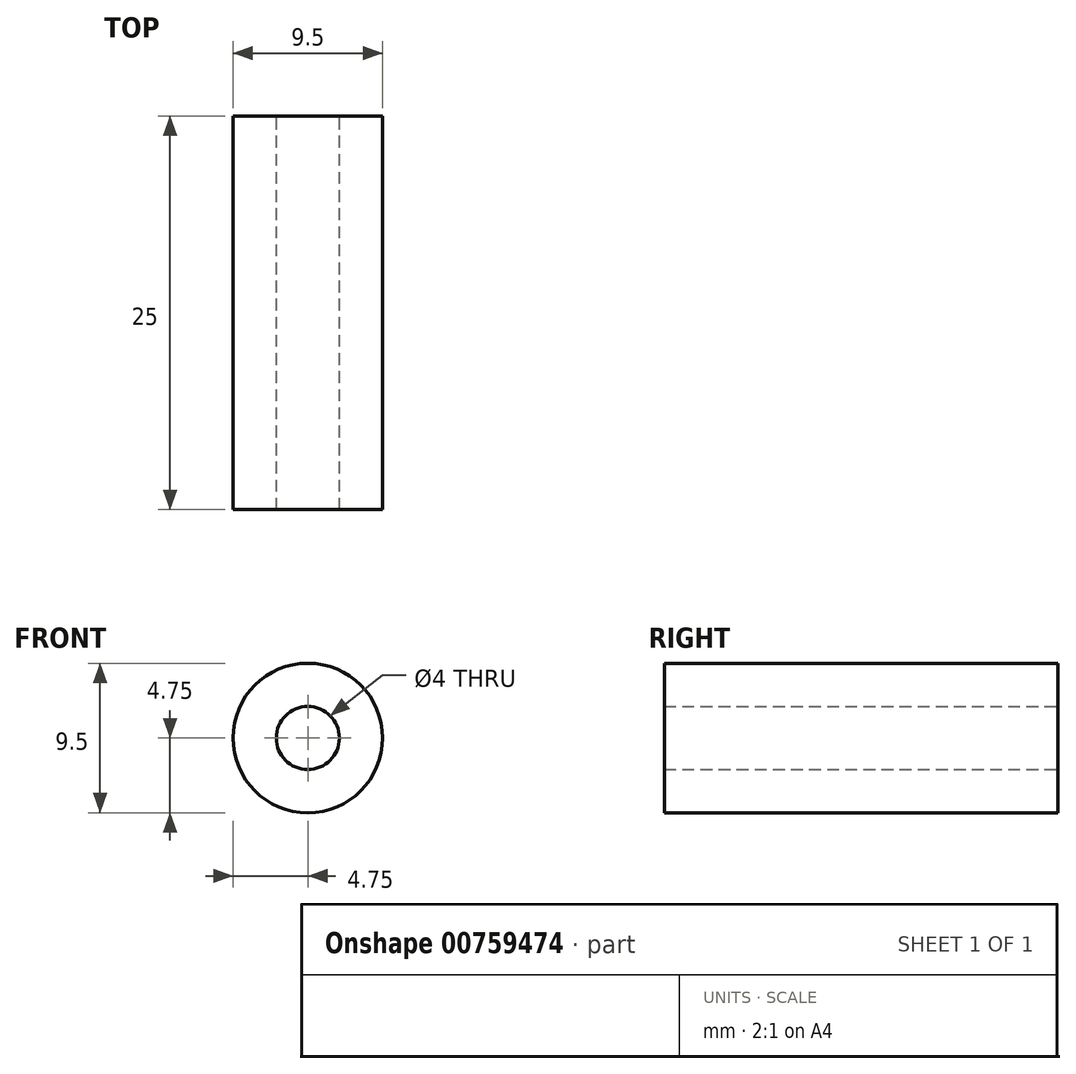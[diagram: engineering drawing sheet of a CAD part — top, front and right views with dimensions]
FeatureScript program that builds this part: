
annotation { "Feature Type Name" : "Feature", "Feature Type Description" : "" }
export const myFeature = defineFeature(function(context is Context, id is Id, definition is map)
    precondition{}
    {
        {
            var Q0;
            Q0=qCreatedBy(makeId("Front.planeOp"),FACE);
            var sketch = newSketch(context, id + "F0", { "sketchPlane" : qUnion([Q0])});
            skCircle(sketch, "E0", {"center": v(0, 0) * mm, "radius": 4.75 * mm});
            skCircle(sketch, "E1", {"center": v(0, 0) * mm, "radius": 2 * mm});
            skSolve(sketch);
        }
        {
            var Q0;
            Q0=makeQuery(id+"F0.imprint","IMPRINT",FACE,{"disambiguationData":[TD([[makeQuery(id+"F0.imprint","IMPRINT",EDGE,{"derivedFrom":sQuery(id+"F0.wireOp",EDGE,"E0")}),1.0]])]});
            extrude(context, id + "F1", {"entities" : qUnion([Q0]), "depth" : 25 * mm, "offsetDistance" : 25 * mm});
        }
    });
